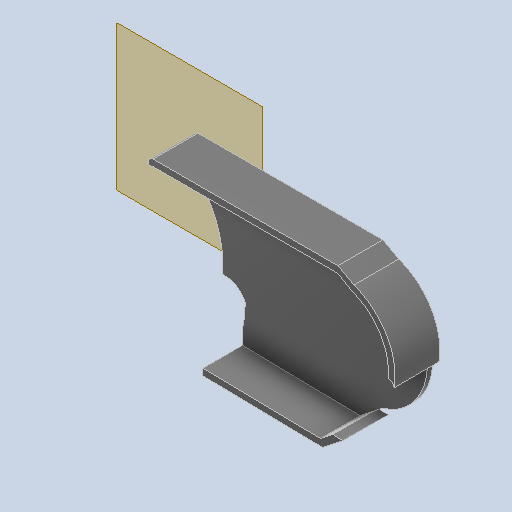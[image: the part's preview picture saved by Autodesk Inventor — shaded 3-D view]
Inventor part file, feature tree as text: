
AUTODESK INVENTOR PART (.ipt)
format: ipt  version: 2022 (Build 260153000, 153)  size: 354,816 bytes
history: native  units: in
note: dims shown in document units (in); Inventor stores cm internally (conversion verified against a paired STEP export)
features: plane x2, extrude x2, sketch x2, other x1
ambient origin geometry x8: Origin, YZ Plane, XZ Plane, XY Plane, X Axis, Y Axis, Z Axis, Center Point
bodies: Body1 (feature_tree)
feature tree (7):
  other  "Sólido1"
  plane  "Plano de trabajo2"
  extrude  "Extrusión2"  Depth=0.0394in
  plane  "Plano de trabajo1"
  extrude  "Extrusión3"  Depth=0.0394in
  sketch  "Boceto2"  dims[d8=0.0315in d9=0.0in d10=0.0394in d11=0.0394in d12=0.0394in]
  sketch  "Boceto3"  dims[d13=0.2677in d14=0.0in d15=0.0394in d16=0.0344in d17=0.0197in d18=0.0344in]
